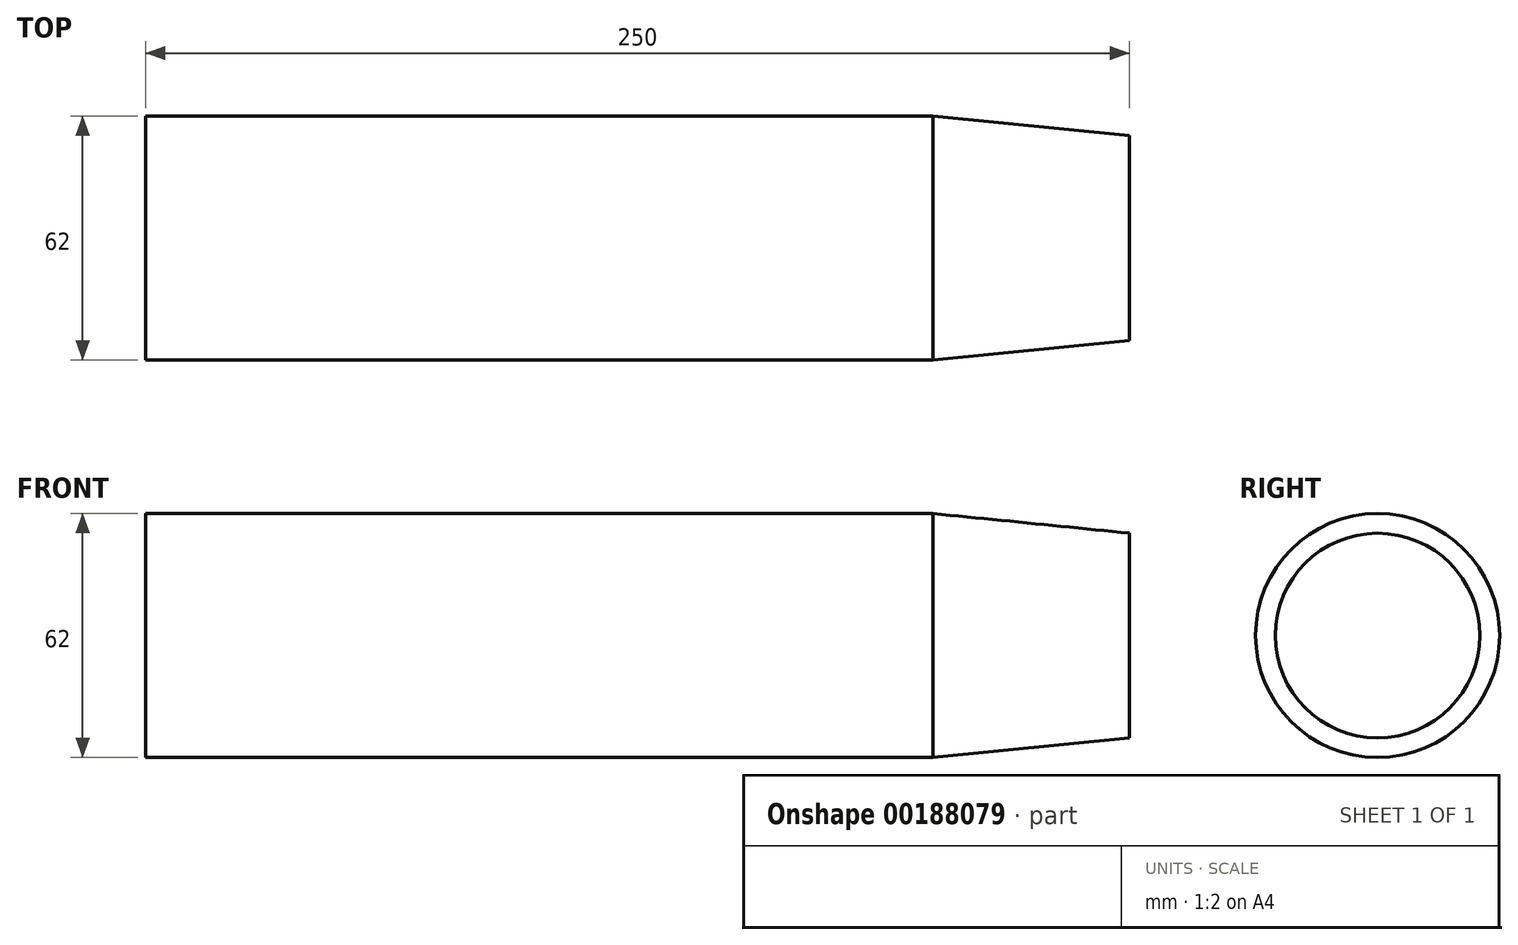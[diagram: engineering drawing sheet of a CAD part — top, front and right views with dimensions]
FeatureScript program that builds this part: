
annotation { "Feature Type Name" : "Feature", "Feature Type Description" : "" }
export const myFeature = defineFeature(function(context is Context, id is Id, definition is map)
    precondition{}
    {
        {
            var Q0;
            Q0=qCreatedBy(makeId("Front.planeOp"),FACE);
            var sketch = newSketch(context, id + "F0", { "sketchPlane" : qUnion([Q0])});
            skLineSegment(sketch, "E0", {"start": v(0, 0) * mm, "end": v(100, 0) * mm});
            skLineSegment(sketch, "E1", {"start": v(0, 0) * mm, "end": v(0, -31) * mm});
            skLineSegment(sketch, "E2", {"start": v(0, -31) * mm, "end": v(150, -31) * mm});
            skLineSegment(sketch, "E3", {"start": v(150, -31) * mm, "end": v(150, -5) * mm});
            skLineSegment(sketch, "E4", {"start": v(150, -5) * mm, "end": v(100, 0) * mm});
            skLineSegment(sketch, "E5", {"start": v(0, 0) * mm, "end": v(-100, 0) * mm});
            skLineSegment(sketch, "E6", {"start": v(-100, 0) * mm, "end": v(-100, -31) * mm});
            skLineSegment(sketch, "E7", {"start": v(-100, -31) * mm, "end": v(0, -31) * mm});
            skSolve(sketch);
        }
        {
            var Q0;
            Q0=qSketchRegion(id+"F0",true);
            var Q1;
            Q1=sQuery(id+"F0.wireOp",EDGE,"E2");
            revolve(context, id + "F1", {"entities" : qUnion([Q0]), "axis" : qUnion([Q1]), "revolveType" : RevolveType.FULL});
        }
    });
